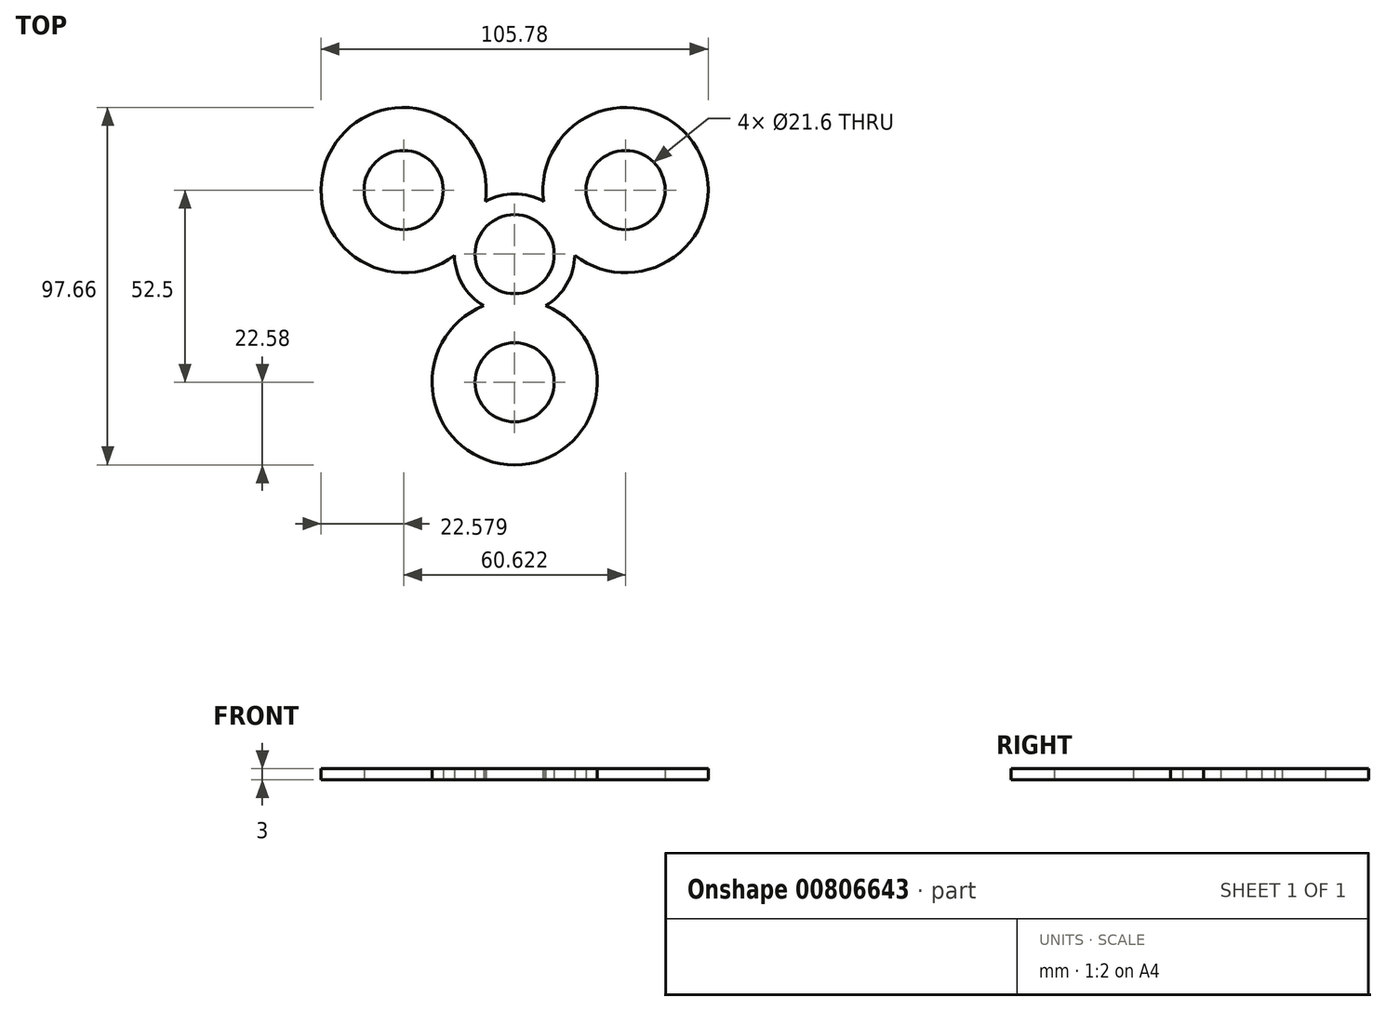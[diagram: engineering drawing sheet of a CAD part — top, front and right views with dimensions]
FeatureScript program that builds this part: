
annotation { "Feature Type Name" : "Feature", "Feature Type Description" : "" }
export const myFeature = defineFeature(function(context is Context, id is Id, definition is map)
    precondition{}
    {
        {
            var Q0;
            Q0=qCreatedBy(makeId("Top.planeOp"),FACE);
            var sketch = newSketch(context, id + "F0", { "sketchPlane" : qUnion([Q0])});
            skArc(sketch, "E0", {"start": v(-9.35, -5.4) * mm, "mid": v(0, -10.8) * mm, "end": v(9.35, -5.4) * mm});
            skArc(sketch, "E1", {"start": v(8.5, -14.08) * mm, "mid": v(11.74, -11.51) * mm, "end": v(14.24, -8.22) * mm});
            skCircle(sketch, "E2", {"center": v(0, -35) * mm, "radius": 10.8 * mm});
            skArc(sketch, "E3", {"start": v(-8.5, -14.08) * mm, "mid": v(0, -57.58) * mm, "end": v(8.5, -14.08) * mm});
            skArc(sketch, "E4.trimOffspring", {"start": v(-14.24, -8.22) * mm, "mid": v(-11.74, -11.51) * mm, "end": v(-8.5, -14.08) * mm});
            skCircle(sketch, "E5.1.0", {"center": v(30.31, 17.5) * mm, "radius": 10.8 * mm});
            skArc(sketch, "E5.1.1", {"start": v(14.24, -8.22) * mm, "mid": v(15.84, -4.4) * mm, "end": v(16.44, -0.31) * mm});
            skArc(sketch, "E5.1.2", {"start": v(7.95, 14.4) * mm, "mid": v(4.1, 15.92) * mm, "end": v(0, 16.44) * mm});
            skArc(sketch, "E5.1.3", {"start": v(9.35, -5.4) * mm, "mid": v(9.35, 5.4) * mm, "end": v(0, 10.8) * mm});
            skArc(sketch, "E5.1.4", {"start": v(16.44, -0.31) * mm, "mid": v(49.86, 28.79) * mm, "end": v(7.95, 14.4) * mm});
            skCircle(sketch, "E5.2.0", {"center": v(-30.31, 17.5) * mm, "radius": 10.8 * mm});
            skArc(sketch, "E5.2.1", {"start": v(0, 16.44) * mm, "mid": v(-4.1, 15.92) * mm, "end": v(-7.95, 14.4) * mm});
            skArc(sketch, "E5.2.2", {"start": v(-16.44, -0.31) * mm, "mid": v(-15.84, -4.4) * mm, "end": v(-14.24, -8.22) * mm});
            skArc(sketch, "E5.2.3", {"start": v(0, 10.8) * mm, "mid": v(-9.35, 5.4) * mm, "end": v(-9.35, -5.4) * mm});
            skArc(sketch, "E5.2.4", {"start": v(-7.95, 14.4) * mm, "mid": v(-49.86, 28.79) * mm, "end": v(-16.44, -0.31) * mm});
            skSolve(sketch);
        }
        {
            var Q0;
            Q0=makeQuery(id+"F0.imprint","IMPRINT",FACE,{"disambiguationData":[TD([[makeQuery(id+"F0.imprint","IMPRINT",EDGE,{"derivedFrom":sQuery(id+"F0.wireOp",EDGE,"E0")}),-1.0]])]});
            extrude(context, id + "F1", {"entities" : qUnion([Q0]), "depth" : 3 * mm, "offsetDistance" : 25 * mm});
        }
    });
